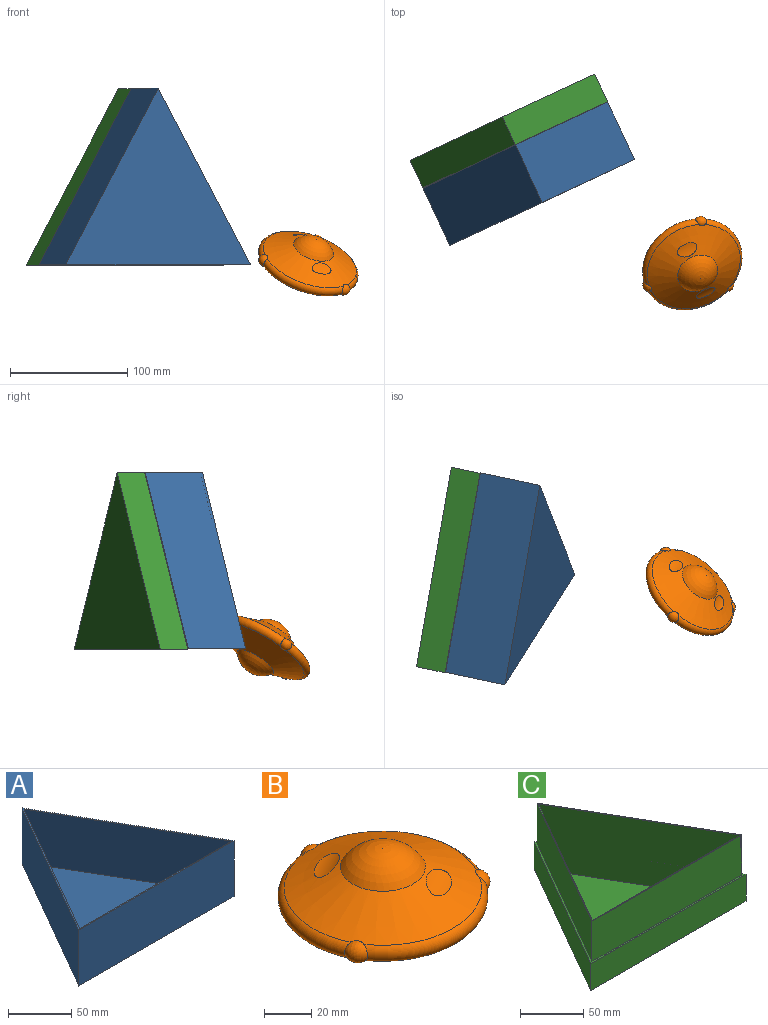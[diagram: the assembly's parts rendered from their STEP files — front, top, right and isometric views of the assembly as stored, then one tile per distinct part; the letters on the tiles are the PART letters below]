
ASSEMBLY  parts=3 mates=1
PART A: 9 faces, bbox 174x150.7x54 mm
  f0: plane 174x54mm, normal (0,-1,0), area 9396mm2, adj f1,f2,f3,f7
  f1: plane 150.69x87mm, normal (0.87,0.5,0), area 9396mm2, adj f0,f2,f3,f7
  f2: plane 150.69x87mm, normal (-0.87,0.5,0), area 9396mm2, adj f0,f1,f3,f7
  f3: plane 174x150.69mm, normal (0,0,-1), area 13109.9mm2, adj f0,f1,f2
  f4: plane 147.22x85mm, normal (-0.87,-0.5,0), area 8840mm2, adj f5,f6,f7,f8
  f5: plane 170x52mm, normal (0,1,0), area 8840mm2, adj f4,f6,f7,f8
  f6: plane 147.22x85mm, normal (0.87,-0.5,0), area 8840mm2, adj f4,f5,f7,f8
  f7: plane 174x150.69mm, normal (0,0,1), area 595.8mm2, adj f0,f1,f2,f4,f5,f6
  f8: plane 170x147.22mm, normal (0,0,1), area 12514.1mm2, adj f4,f5,f6
PART B: 26 faces, bbox 95.8x95.7x49.9 mm
  f0: cone r=17.93mm half-angle=64.8deg, axis (0,0,-1), area 4562.4mm2, adj f1,f2,f4,f6,f7,f8,f9,f10
  f1: torus R=39.65mm, axis (0,0,1), area 841.8mm2, adj f0,f3,f7,f9
  f2: torus R=39.65mm, axis (0,0,1), area 841.8mm2, adj f0,f3,f8,f9
  f3: cone r=41.58mm half-angle=64.8deg, axis (0,0,1), area 4871.6mm2, adj f1,f2,f4,f5,f7,f8,f9
  f4: torus R=39.65mm, axis (0,0,1), area 841.8mm2, adj f0,f3,f7,f8
  f5: sphere r=21.5mm, area 1301.1mm2, adj f3
  f6: sphere r=21.5mm, area 1301.1mm2, adj f0
  f7: revolved ~9.97x9.55mm, area 140.2mm2, adj f0,f1,f3,f4
  f8: revolved ~10x9.55mm, area 140.2mm2, adj f0,f2,f3,f4
  f9: revolved ~10x9.55mm, area 140.2mm2, adj f0,f1,f2,f3
  f10: cylinder r=22.93mm len=20.42mm, axis (0.87,0.5,0), area 154.5mm2, adj f0,f11
  f11: plane 2.88x1.73mm, normal (0.37,-0.64,-0.67), area 0.1mm2, adj f0,f10
  f12: plane 2.88x1.73mm, normal (-0.37,0.64,-0.67), area 0.1mm2, adj f0,f13
  f13: cylinder r=22.93mm len=20.43mm, axis (0.87,0.5,0), area 154.6mm2, adj f0,f12
  f14: cone r=39.65mm half-angle=64.8deg, axis (0,0,-1), area 461.8mm2, adj f15,f16,f17,f18,f19
  f15: plane 79.3x79.2mm, normal (0,0,1), area 714.7mm2, adj f14,f16,f17,f18,f19
  f16: torus R=39.65mm, axis (0,0,1), area 360.6mm2, adj f14,f15
  f17: revolved ~5.95x1.22mm, area 2.6mm2, adj f14,f15
  f18: revolved ~5.48x3.55mm, area 2.6mm2, adj f14,f15
  f19: revolved ~5.48x3.55mm, area 2.6mm2, adj f14,f15
  f20: revolved ~6x5.47mm, area 32.7mm2, adj f21
  f21: torus R=39.65mm, axis (0,0,1), area 27.7mm2, adj f20
  f22: revolved ~6x5.45mm, area 32.7mm2, adj f23
  f23: torus R=39.65mm, axis (0,0,1), area 27.7mm2, adj f22
  f24: revolved ~6x5.45mm, area 32.7mm2, adj f25
  f25: torus R=39.65mm, axis (0,0,1), area 27.7mm2, adj f24
PART C: 13 faces, bbox 174x150.7x65 mm
  f0: plane 168x145.49mm, normal (0,0,1), area 361mm2, adj f1,f2,f3,f5,f6,f7
  f1: plane 143.33x82.75mm, normal (-0.87,-0.5,0), area 10426.5mm2, adj f0,f2,f3,f4
  f2: plane 165.5x63mm, normal (0,1,0), area 10426.5mm2, adj f0,f1,f3,f4
  f3: plane 143.33x82.75mm, normal (0.87,-0.5,0), area 10426.5mm2, adj f0,f1,f2,f4
  f4: plane 165.5x143.33mm, normal (0,0,1), area 11860.3mm2, adj f1,f2,f3
  f5: plane 145.49x84mm, normal (-0.87,0.5,0), area 6552mm2, adj f0,f6,f7,f8
  f6: plane 145.49x84mm, normal (0.87,0.5,0), area 6552mm2, adj f0,f5,f7,f8
  f7: plane 168x39mm, normal (0,-1,0), area 6552mm2, adj f0,f5,f6,f8
  f8: plane 174x150.69mm, normal (0,0,1), area 888.5mm2, adj f5,f6,f7,f10,f11,f12
  f9: plane 174x150.69mm, normal (0,0,-1), area 13109.9mm2, adj f10,f11,f12
  f10: plane 150.69x87mm, normal (-0.87,0.5,0), area 4524mm2, adj f8,f9,f11,f12
  f11: plane 150.69x87mm, normal (0.87,0.5,0), area 4524mm2, adj f8,f9,f10,f12
  f12: plane 174x26mm, normal (0,-1,0), area 4524mm2, adj f8,f9,f10,f11
PLACE A rot(axis=(0.15,-0.7,-0.7),162.4deg) t=(29.35,81.44,-37.81)mm fixed
PLACE B rot(axis=(0.83,0.54,-0.15),35.9deg) t=(157.5,28.67,-87.03)mm
PLACE C rot(axis=(0.95,0.21,0.21),92.7deg) t=(-4.61,154.27,-38.39)mm
MATE planar C.f7 <-> A.f5  axis (0,0,-1) through (14.62,113.03,-86.89)mm
